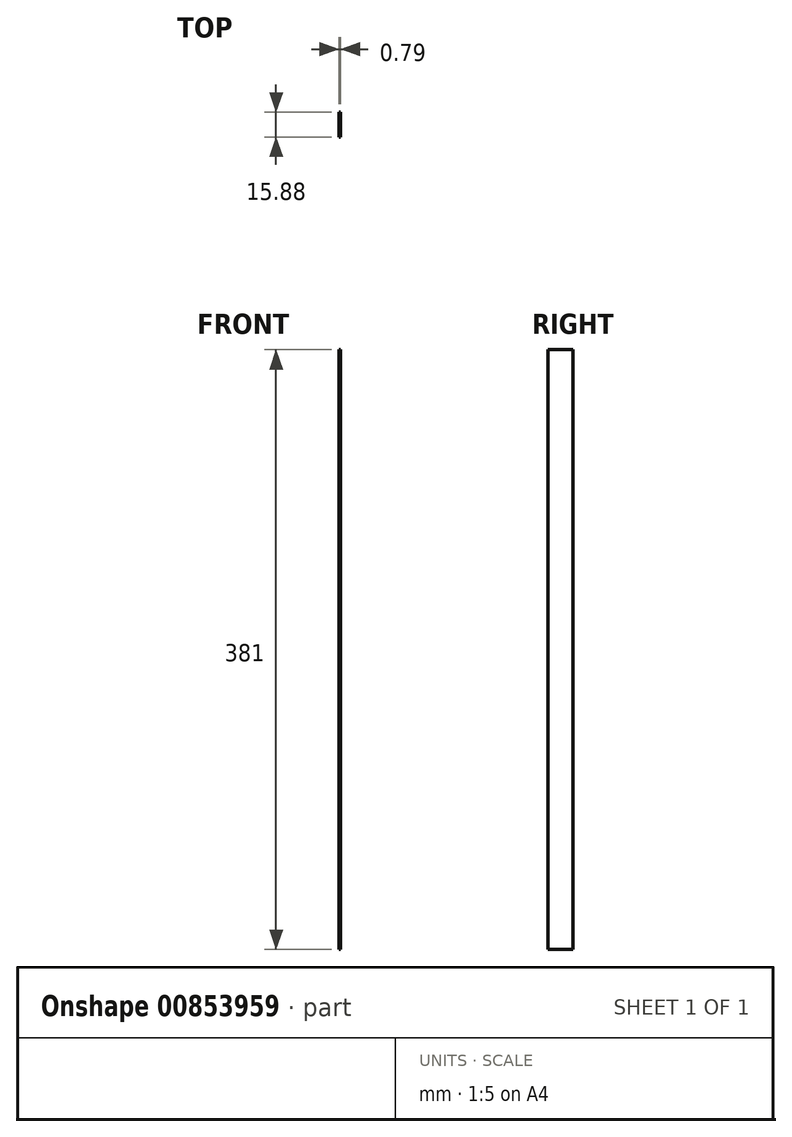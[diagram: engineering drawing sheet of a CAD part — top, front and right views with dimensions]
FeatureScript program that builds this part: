
annotation { "Feature Type Name" : "Feature", "Feature Type Description" : "" }
export const myFeature = defineFeature(function(context is Context, id is Id, definition is map)
    precondition{}
    {
        {
            var Q0;
            Q0=qCreatedBy(makeId("Front.planeOp"),FACE);
            var sketch = newSketch(context, id + "F0", { "sketchPlane" : qUnion([Q0])});
            skLineSegment(sketch, "E0.bottom", {"start": v(0, 0) * mm, "end": v(0.8, 0) * mm});
            skLineSegment(sketch, "E0.top", {"start": v(0, 381) * mm, "end": v(0.8, 381) * mm});
            skLineSegment(sketch, "E0.left", {"start": v(0, 0) * mm, "end": v(0, 381) * mm});
            skLineSegment(sketch, "E0.right", {"start": v(0.8, 0) * mm, "end": v(0.8, 381) * mm});
            skSolve(sketch);
        }
        {
            var Q0;
            Q0=makeQuery(id+"F0.imprint","IMPRINT",FACE,{"disambiguationData":[TD([[makeQuery(id+"F0.imprint","IMPRINT",EDGE,{"derivedFrom":sQuery(id+"F0.wireOp",EDGE,"E0.bottom")}),1.0]])]});
            extrude(context, id + "F1", {"entities" : qUnion([Q0]), "oppositeDirection" : true, "depth" : 15.88 * mm, "offsetDistance" : 25.4 * mm});
        }
    });
